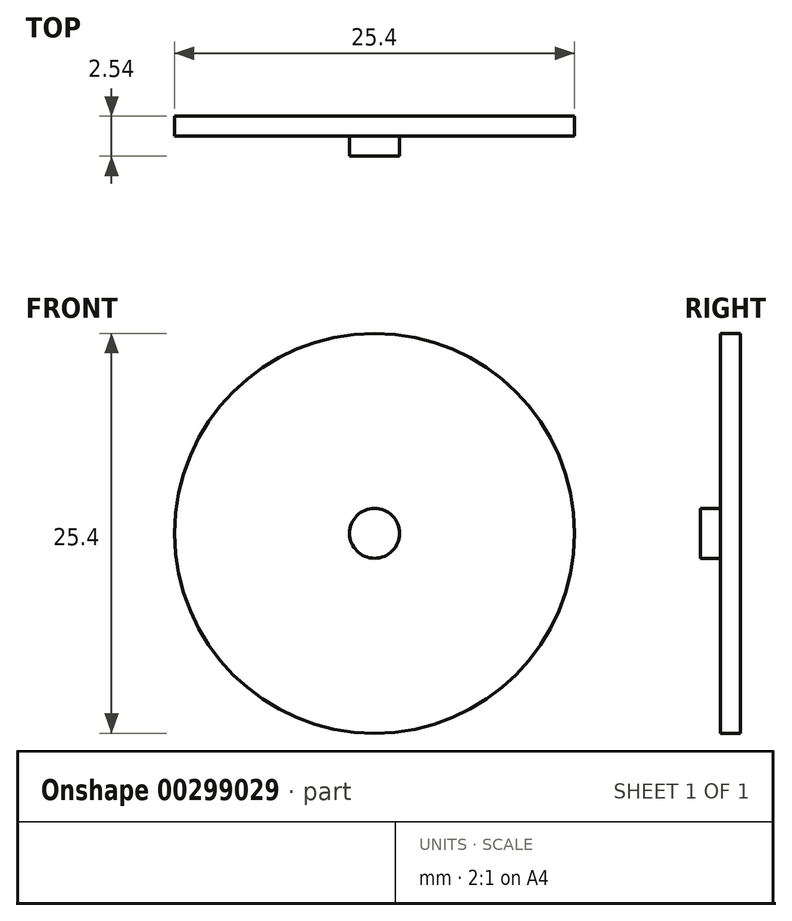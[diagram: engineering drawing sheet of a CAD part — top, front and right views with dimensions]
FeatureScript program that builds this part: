
annotation { "Feature Type Name" : "Feature", "Feature Type Description" : "" }
export const myFeature = defineFeature(function(context is Context, id is Id, definition is map)
    precondition{}
    {
        {
            var Q0;
            Q0=qCreatedBy(makeId("Front.planeOp"),FACE);
            var sketch = newSketch(context, id + "F0", { "sketchPlane" : qUnion([Q0])});
            skCircle(sketch, "E0", {"center": v(-6.17, 0) * mm, "radius": 12.7 * mm});
            skLineSegment(sketch, "E1", {"start": v(-6.17, -12.7) * mm, "end": v(-6.17, 12.7) * mm});
            skLineSegment(sketch, "E2", {"start": v(6.53, 0) * mm, "end": v(-18.87, 0) * mm});
            skLineSegment(sketch, "E3", {"start": v(-6.17, 0) * mm, "end": v(-15.15, 8.98) * mm});
            skLineSegment(sketch, "E4", {"start": v(-6.17, 0) * mm, "end": v(2.81, -8.98) * mm});
            skLineSegment(sketch, "E5", {"start": v(-6.17, 0) * mm, "end": v(2.81, 8.98) * mm});
            skLineSegment(sketch, "E6", {"start": v(-6.17, 0) * mm, "end": v(-15.15, -8.98) * mm});
            skCircle(sketch, "E7", {"center": v(-6.17, 0) * mm, "radius": 11.43 * mm});
            skSolve(sketch);
        }
        {
            var Q0;
            {var subQ0=sQuery(id+"F0.wireOp",EDGE,"E1");var subQ1=sQuery(id+"F0.wireOp",EDGE,"E0");var subQ2=makeQuery(id+"F0.imprint","INTERSECT",VERTEX,{"disambiguationData":[OD(1.0)],"derivedFrom":[subQ1,subQ0]});Q0=makeQuery(id+"F0.imprint","IMPRINT",FACE,{"disambiguationData":[TD([[makeQuery(id+"F0.imprint","IMPRINT",EDGE,{"disambiguationData":[TD([[subQ2,-1.0]])],"derivedFrom":subQ1}),1.0]])]});}
            var Q1;
            {var subQ0=sQuery(id+"F0.wireOp",EDGE,"E1");var subQ1=sQuery(id+"F0.wireOp",EDGE,"E0");var subQ2=makeQuery(id+"F0.imprint","INTERSECT",VERTEX,{"disambiguationData":[OD(1.0)],"derivedFrom":[subQ1,subQ0]});Q1=makeQuery(id+"F0.imprint","IMPRINT",FACE,{"disambiguationData":[TD([[makeQuery(id+"F0.imprint","IMPRINT",EDGE,{"disambiguationData":[TD([[subQ2,1.0]])],"derivedFrom":subQ1}),1.0]])]});}
            var Q2;
            {var subQ0=sQuery(id+"F0.wireOp",EDGE,"E2");var subQ1=sQuery(id+"F0.wireOp",EDGE,"E0");var subQ2=makeQuery(id+"F0.imprint","INTERSECT",VERTEX,{"disambiguationData":[OD(0.0)],"derivedFrom":[subQ1,subQ0]});Q2=makeQuery(id+"F0.imprint","IMPRINT",FACE,{"disambiguationData":[TD([[makeQuery(id+"F0.imprint","IMPRINT",EDGE,{"disambiguationData":[TD([[subQ2,-1.0]])],"derivedFrom":subQ1}),1.0]])]});}
            var Q3;
            {var subQ0=sQuery(id+"F0.wireOp",EDGE,"E2");var subQ1=sQuery(id+"F0.wireOp",EDGE,"E0");var subQ2=makeQuery(id+"F0.imprint","INTERSECT",VERTEX,{"disambiguationData":[OD(0.0)],"derivedFrom":[subQ1,subQ0]});Q3=makeQuery(id+"F0.imprint","IMPRINT",FACE,{"disambiguationData":[TD([[makeQuery(id+"F0.imprint","IMPRINT",EDGE,{"disambiguationData":[TD([[subQ2,1.0]])],"derivedFrom":subQ1}),1.0]])]});}
            var Q4;
            {var subQ0=sQuery(id+"F0.wireOp",EDGE,"E1");var subQ1=sQuery(id+"F0.wireOp",EDGE,"E0");var subQ2=makeQuery(id+"F0.imprint","INTERSECT",VERTEX,{"disambiguationData":[OD(0.0)],"derivedFrom":[subQ1,subQ0]});Q4=makeQuery(id+"F0.imprint","IMPRINT",FACE,{"disambiguationData":[TD([[makeQuery(id+"F0.imprint","IMPRINT",EDGE,{"disambiguationData":[TD([[subQ2,-1.0]])],"derivedFrom":subQ1}),1.0]])]});}
            var Q5;
            {var subQ0=sQuery(id+"F0.wireOp",EDGE,"E1");var subQ1=sQuery(id+"F0.wireOp",EDGE,"E0");var subQ2=makeQuery(id+"F0.imprint","INTERSECT",VERTEX,{"disambiguationData":[OD(0.0)],"derivedFrom":[subQ1,subQ0]});Q5=makeQuery(id+"F0.imprint","IMPRINT",FACE,{"disambiguationData":[TD([[makeQuery(id+"F0.imprint","IMPRINT",EDGE,{"disambiguationData":[TD([[subQ2,1.0]])],"derivedFrom":subQ1}),1.0]])]});}
            var Q6;
            {var subQ0=sQuery(id+"F0.wireOp",EDGE,"E2");var subQ1=sQuery(id+"F0.wireOp",EDGE,"E0");var subQ2=makeQuery(id+"F0.imprint","INTERSECT",VERTEX,{"disambiguationData":[OD(1.0)],"derivedFrom":[subQ1,subQ0]});Q6=makeQuery(id+"F0.imprint","IMPRINT",FACE,{"disambiguationData":[TD([[makeQuery(id+"F0.imprint","IMPRINT",EDGE,{"disambiguationData":[TD([[subQ2,-1.0]])],"derivedFrom":subQ1}),1.0]])]});}
            var Q7;
            {var subQ0=sQuery(id+"F0.wireOp",EDGE,"E2");var subQ1=sQuery(id+"F0.wireOp",EDGE,"E0");var subQ2=makeQuery(id+"F0.imprint","INTERSECT",VERTEX,{"disambiguationData":[OD(1.0)],"derivedFrom":[subQ1,subQ0]});Q7=makeQuery(id+"F0.imprint","IMPRINT",FACE,{"disambiguationData":[TD([[makeQuery(id+"F0.imprint","IMPRINT",EDGE,{"disambiguationData":[TD([[subQ2,1.0]])],"derivedFrom":subQ1}),1.0]])]});}
            var Q8;
            {var subQ1=sQuery(id+"F0.wireOp",EDGE,"E1");var subQ3=sQuery(id+"F0.wireOp",EDGE,"E7");var subQ4=makeQuery(id+"F0.imprint","INTERSECT",VERTEX,{"disambiguationData":[OD(1.0)],"derivedFrom":[subQ1,subQ3]});Q8=makeQuery(id+"F0.imprint","IMPRINT",FACE,{"disambiguationData":[TD([[makeQuery(id+"F0.imprint","IMPRINT",EDGE,{"disambiguationData":[TD([[subQ4,1.0]])],"derivedFrom":subQ3}),1.0]])]});}
            var Q9;
            {var subQ1=sQuery(id+"F0.wireOp",EDGE,"E2");var subQ3=sQuery(id+"F0.wireOp",EDGE,"E7");var subQ4=makeQuery(id+"F0.imprint","INTERSECT",VERTEX,{"disambiguationData":[OD(0.0)],"derivedFrom":[subQ1,subQ3]});Q9=makeQuery(id+"F0.imprint","IMPRINT",FACE,{"disambiguationData":[TD([[makeQuery(id+"F0.imprint","IMPRINT",EDGE,{"disambiguationData":[TD([[subQ4,-1.0]])],"derivedFrom":subQ3}),1.0]])]});}
            var Q10;
            {var subQ1=sQuery(id+"F0.wireOp",EDGE,"E2");var subQ3=sQuery(id+"F0.wireOp",EDGE,"E7");var subQ4=makeQuery(id+"F0.imprint","INTERSECT",VERTEX,{"disambiguationData":[OD(0.0)],"derivedFrom":[subQ1,subQ3]});Q10=makeQuery(id+"F0.imprint","IMPRINT",FACE,{"disambiguationData":[TD([[makeQuery(id+"F0.imprint","IMPRINT",EDGE,{"disambiguationData":[TD([[subQ4,1.0]])],"derivedFrom":subQ3}),1.0]])]});}
            var Q11;
            {var subQ1=sQuery(id+"F0.wireOp",EDGE,"E1");var subQ3=sQuery(id+"F0.wireOp",EDGE,"E7");var subQ4=makeQuery(id+"F0.imprint","INTERSECT",VERTEX,{"disambiguationData":[OD(0.0)],"derivedFrom":[subQ1,subQ3]});Q11=makeQuery(id+"F0.imprint","IMPRINT",FACE,{"disambiguationData":[TD([[makeQuery(id+"F0.imprint","IMPRINT",EDGE,{"disambiguationData":[TD([[subQ4,-1.0]])],"derivedFrom":subQ3}),1.0]])]});}
            var Q12;
            {var subQ1=sQuery(id+"F0.wireOp",EDGE,"E1");var subQ3=sQuery(id+"F0.wireOp",EDGE,"E7");var subQ4=makeQuery(id+"F0.imprint","INTERSECT",VERTEX,{"disambiguationData":[OD(0.0)],"derivedFrom":[subQ1,subQ3]});Q12=makeQuery(id+"F0.imprint","IMPRINT",FACE,{"disambiguationData":[TD([[makeQuery(id+"F0.imprint","IMPRINT",EDGE,{"disambiguationData":[TD([[subQ4,1.0]])],"derivedFrom":subQ3}),1.0]])]});}
            var Q13;
            {var subQ1=sQuery(id+"F0.wireOp",EDGE,"E1");var subQ3=sQuery(id+"F0.wireOp",EDGE,"E7");var subQ4=makeQuery(id+"F0.imprint","INTERSECT",VERTEX,{"disambiguationData":[OD(1.0)],"derivedFrom":[subQ1,subQ3]});Q13=makeQuery(id+"F0.imprint","IMPRINT",FACE,{"disambiguationData":[TD([[makeQuery(id+"F0.imprint","IMPRINT",EDGE,{"disambiguationData":[TD([[subQ4,-1.0]])],"derivedFrom":subQ3}),1.0]])]});}
            var Q14;
            {var subQ1=sQuery(id+"F0.wireOp",EDGE,"E2");var subQ3=sQuery(id+"F0.wireOp",EDGE,"E7");var subQ4=makeQuery(id+"F0.imprint","INTERSECT",VERTEX,{"disambiguationData":[OD(1.0)],"derivedFrom":[subQ1,subQ3]});Q14=makeQuery(id+"F0.imprint","IMPRINT",FACE,{"disambiguationData":[TD([[makeQuery(id+"F0.imprint","IMPRINT",EDGE,{"disambiguationData":[TD([[subQ4,1.0]])],"derivedFrom":subQ3}),1.0]])]});}
            var Q15;
            {var subQ1=sQuery(id+"F0.wireOp",EDGE,"E2");var subQ3=sQuery(id+"F0.wireOp",EDGE,"E7");var subQ4=makeQuery(id+"F0.imprint","INTERSECT",VERTEX,{"disambiguationData":[OD(1.0)],"derivedFrom":[subQ1,subQ3]});Q15=makeQuery(id+"F0.imprint","IMPRINT",FACE,{"disambiguationData":[TD([[makeQuery(id+"F0.imprint","IMPRINT",EDGE,{"disambiguationData":[TD([[subQ4,-1.0]])],"derivedFrom":subQ3}),1.0]])]});}
            extrude(context, id + "F1", {"entities" : qUnion([Q0, Q1, Q2, Q3, Q4, Q5, Q6, Q7, Q8, Q9, Q10, Q11, Q12, Q13, Q14, Q15]), "oppositeDirection" : true, "depth" : 1.27 * mm});
        }
        {
            var Q0;
            Q0=qCreatedBy(makeId("Front.planeOp"),FACE);
            var sketch = newSketch(context, id + "F2", { "sketchPlane" : qUnion([Q0])});
            skPoint(sketch, "E8.0", {"position": v(-6.17, 0) * mm});
            skCircle(sketch, "E9", {"center": v(-6.17, 0) * mm, "radius": 1.59 * mm});
            skSolve(sketch);
        }
        {
            var Q0;
            Q0 = qSketchRegion(id + "F2", true);
            extrude(context, id + "F3", {"entities" : qUnion([Q0]), "operationType" : NewBodyOperationType.ADD, "depth" : 1.27 * mm});
        }
    });
